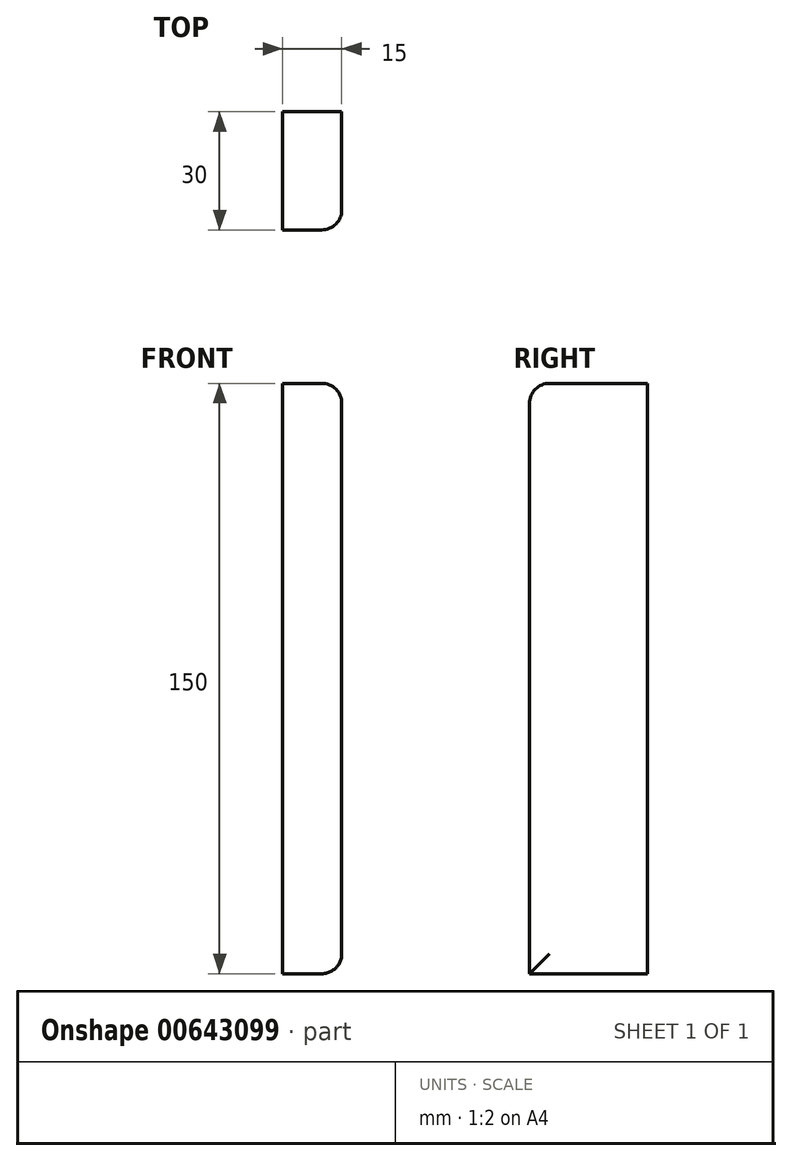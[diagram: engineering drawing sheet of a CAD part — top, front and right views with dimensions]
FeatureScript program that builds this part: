
annotation { "Feature Type Name" : "Feature", "Feature Type Description" : "" }
export const myFeature = defineFeature(function(context is Context, id is Id, definition is map)
    precondition{}
    {
        {
            var Q0;
            Q0=qCreatedBy(makeId("Top.planeOp"),FACE);
            var sketch = newSketch(context, id + "F0", { "sketchPlane" : qUnion([Q0])});
            skLineSegment(sketch, "E0.bottom", {"start": v(-8.12, 22.37) * mm, "end": v(6.88, 22.37) * mm});
            skLineSegment(sketch, "E0.top", {"start": v(-8.12, -7.63) * mm, "end": v(6.88, -7.63) * mm});
            skLineSegment(sketch, "E0.left", {"start": v(-8.12, 22.37) * mm, "end": v(-8.12, -7.63) * mm});
            skLineSegment(sketch, "E0.right", {"start": v(6.88, 22.37) * mm, "end": v(6.88, -7.63) * mm});
            skSolve(sketch);
        }
        {
            var Q0;
            Q0=makeQuery(id+"F0.imprint","IMPRINT",FACE,{"disambiguationData":[TD([[makeQuery(id+"F0.imprint","IMPRINT",EDGE,{"derivedFrom":sQuery(id+"F0.wireOp",EDGE,"E0.bottom")}),-1.0]])]});
            extrude(context, id + "F1", {"entities" : qUnion([Q0]), "depth" : 150 * mm, "offsetDistance" : 25.4 * mm});
        }
        {
            var Q0;
            Q0=makeQuery(id+"F1.opExtrude","SWEPT_EDGE",EDGE,{"disambiguationData":[OSD([sQuery(id+"F0.wireOp",EDGE,"E0.top"),sQuery(id+"F0.wireOp",EDGE,"E0.right")])]});
            var Q1;
            Q1=makeQuery(id+"F1.opExtrude","CAP_EDGE",EDGE,{"disambiguationData":[OSD([sQuery(id+"F0.wireOp",EDGE,"E0.right")])],"isStart":true});
            fillet(context, id + "F2", {"entities" : qUnion([Q0, Q1]), "radius" : 5.08 * mm, "tangentPropagation" : true, "allowEdgeOverflow" : false});
        }
        {
            var Q0;
            Q0=makeQuery(id+"F1.opExtrude","CAP_EDGE",EDGE,{"disambiguationData":[OSD([sQuery(id+"F0.wireOp",EDGE,"E0.right")])],"isStart":false});
            fillet(context, id + "F3", {"entities" : qUnion([Q0]), "radius" : 5.08 * mm, "tangentPropagation" : true, "allowEdgeOverflow" : false});
        }
    });
